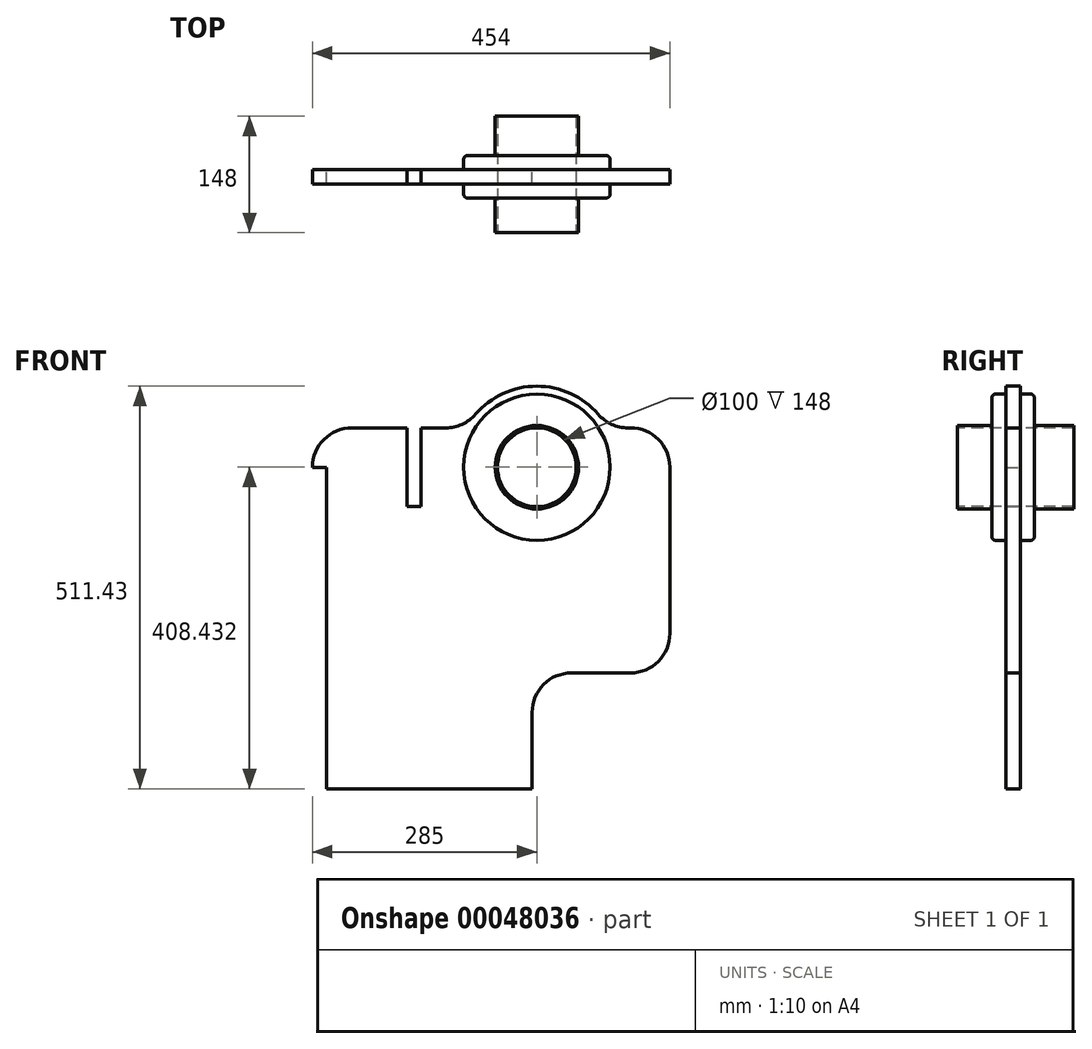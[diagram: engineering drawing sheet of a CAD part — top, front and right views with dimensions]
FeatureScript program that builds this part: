
annotation { "Feature Type Name" : "Feature", "Feature Type Description" : "" }
export const myFeature = defineFeature(function(context is Context, id is Id, definition is map)
    precondition{}
    {
        {
            var Q0;
            Q0=qCreatedBy(makeId("Front.planeOp"),FACE);
            var sketch = newSketch(context, id + "F0", { "sketchPlane" : qUnion([Q0])});
            skLineSegment(sketch, "E0", {"start": v(261, 333.88) * mm, "end": v(261, 431) * mm});
            skLineSegment(sketch, "E1", {"start": v(311, 481) * mm, "end": v(386, 481) * mm});
            skLineSegment(sketch, "E2.trimOffspring", {"start": v(436, 531) * mm, "end": v(436, 742.31) * mm});
            skLineSegment(sketch, "E3.0", {"start": v(32, 792.31) * mm, "end": v(102, 792.31) * mm});
            skCircle(sketch, "E4", {"center": v(267, 742.31) * mm, "radius": 53 * mm});
            skArc(sketch, "E5.0", {"start": v(344.96, 809.63) * mm, "mid": v(267, 845.31) * mm, "end": v(189.04, 809.63) * mm});
            skLineSegment(sketch, "E6.trimOffspring", {"start": v(382.8, 792.31) * mm, "end": v(386, 792.31) * mm});
            skPoint(sketch, "E7.visualSharp", {"position": v(357.05, 792.31) * mm});
            skArc(sketch, "E7.filletArc", {"start": v(344.96, 809.63) * mm, "mid": v(361.99, 796.85) * mm, "end": v(382.8, 792.31) * mm});
            skPoint(sketch, "E8.visualSharp", {"position": v(176.95, 792.31) * mm});
            skArc(sketch, "E8.filletArc", {"start": v(151.2, 792.31) * mm, "mid": v(172.01, 796.85) * mm, "end": v(189.04, 809.63) * mm});
            skPoint(sketch, "E9.visualSharp", {"position": v(436, 792.31) * mm});
            skArc(sketch, "E9.filletArc", {"start": v(436, 742.31) * mm, "mid": v(421.36, 777.67) * mm, "end": v(386, 792.31) * mm});
            skPoint(sketch, "E10.visualSharp", {"position": v(436, 481) * mm});
            skArc(sketch, "E10.filletArc", {"start": v(386, 481) * mm, "mid": v(421.36, 495.64) * mm, "end": v(436, 531) * mm});
            skPoint(sketch, "E11.visualSharp", {"position": v(261, 481) * mm});
            skArc(sketch, "E11.filletArc", {"start": v(311, 481) * mm, "mid": v(275.64, 466.36) * mm, "end": v(261, 431) * mm});
            skPoint(sketch, "E12.visualSharp", {"position": v(261, 446.37) * mm});
            skLineSegment(sketch, "E13", {"start": v(102, 792.31) * mm, "end": v(102, 692.31) * mm});
            skLineSegment(sketch, "E14", {"start": v(120, 792.31) * mm, "end": v(120, 692.31) * mm});
            skLineSegment(sketch, "E15", {"start": v(120, 692.31) * mm, "end": v(102, 692.31) * mm});
            skLineSegment(sketch, "E16.trimOffspring", {"start": v(120, 792.31) * mm, "end": v(151.2, 792.31) * mm});
            skLineSegment(sketch, "E17", {"start": v(0, 333.88) * mm, "end": v(0, 741.88) * mm});
            skLineSegment(sketch, "E18.0", {"start": v(0, 333.88) * mm, "end": v(261, 333.88) * mm});
            skLineSegment(sketch, "E19", {"start": v(0, 741.88) * mm, "end": v(-18, 741.88) * mm});
            skLineSegment(sketch, "E20", {"start": v(-18, 742.31) * mm, "end": v(-18, 741.88) * mm});
            skPoint(sketch, "E21.visualSharp", {"position": v(-18, 792.31) * mm});
            skArc(sketch, "E21.filletArc", {"start": v(32, 792.31) * mm, "mid": v(-3.36, 777.67) * mm, "end": v(-18, 742.31) * mm});
            skPoint(sketch, "E22.right.end.orphan", {"position": v(436, 446.37) * mm});
            skSolve(sketch);
        }
        {
            var Q0;
            Q0 = qSketchRegion(id + "F0", true);
            extrude(context, id + "F1", {"entities" : qUnion([Q0]), "depth" : 18 * mm});
        }
        {
            var Q0;
            Q0=makeQuery(id+"F1.opExtrude","CAP_FACE",FACE,{"disambiguationData":[OSD([sQuery(id+"F0.wireOp",EDGE,"E22.bottom"),sQuery(id+"F0.wireOp",EDGE,"E22.left"),sQuery(id+"F0.wireOp",EDGE,"E22.right"),sQuery(id+"F0.wireOp",EDGE,"9340d6fc-de35-4576-8b29-9b64dd72a72c"),sQuery(id+"F0.wireOp",EDGE,"ba2b4bda-3cf2-4f29-995d-d867b2875ad6"),sQuery(id+"F0.wireOp",EDGE,"E0"),sQuery(id+"F0.wireOp",EDGE,"E1"),sQuery(id+"F0.wireOp",EDGE,"E2.trimOffspring"),sQuery(id+"F0.wireOp",EDGE,"1ba28aa8-3367-4210-a1af-1df5a81b962f.filletArc"),sQuery(id+"F0.wireOp",EDGE,"E3.0"),sQuery(id+"F0.wireOp",EDGE,"E4"),sQuery(id+"F0.wireOp",EDGE,"E5.0")])],"isStart":true});
            var sketch = newSketch(context, id + "F2", { "sketchPlane" : qUnion([Q0])});
            skCircle(sketch, "E23.0", {"center": v(-267, 742.31) * mm, "radius": 53 * mm});
            skCircle(sketch, "E24.0", {"center": v(-267, 742.31) * mm, "radius": 50 * mm});
            skSolve(sketch);
        }
        {
            var Q0;
            Q0 = qSketchRegion(id + "F2", true);
            extrude(context, id + "F3", {"entities" : qUnion([Q0]), "operationType" : NewBodyOperationType.ADD, "depth" : 68 * mm, "hasSecondDirection" : true, "secondDirectionOppositeDirection" : true, "secondDirectionDepth" : 80 * mm});
        }
        {
            var Q0;
            Q0=makeQuery(id+"F1.opExtrude","CAP_FACE",FACE,{"disambiguationData":[OSD([sQuery(id+"F0.wireOp",EDGE,"E22.bottom"),sQuery(id+"F0.wireOp",EDGE,"E22.left"),sQuery(id+"F0.wireOp",EDGE,"E22.right"),sQuery(id+"F0.wireOp",EDGE,"9340d6fc-de35-4576-8b29-9b64dd72a72c"),sQuery(id+"F0.wireOp",EDGE,"ba2b4bda-3cf2-4f29-995d-d867b2875ad6"),sQuery(id+"F0.wireOp",EDGE,"E0"),sQuery(id+"F0.wireOp",EDGE,"E1"),sQuery(id+"F0.wireOp",EDGE,"E2.trimOffspring"),sQuery(id+"F0.wireOp",EDGE,"1ba28aa8-3367-4210-a1af-1df5a81b962f.filletArc"),sQuery(id+"F0.wireOp",EDGE,"E3.0"),sQuery(id+"F0.wireOp",EDGE,"E4"),sQuery(id+"F0.wireOp",EDGE,"E5.0")])],"isStart":true});
            var sketch = newSketch(context, id + "F4", { "sketchPlane" : qUnion([Q0])});
            skCircle(sketch, "E25.0", {"center": v(-267, 742.31) * mm, "radius": 53 * mm});
            skCircle(sketch, "E26.0", {"center": v(-267, 742.31) * mm, "radius": 93 * mm});
            skSolve(sketch);
        }
        {
            var Q0;
            Q0 = qSketchRegion(id + "F4", true);
            extrude(context, id + "F5", {"entities" : qUnion([Q0]), "operationType" : NewBodyOperationType.ADD, "depth" : 18 * mm});
        }
        {
            var Q0;
            Q0=makeQuery(id+"F1.opExtrude","CAP_FACE",FACE,{"disambiguationData":[OSD([sQuery(id+"F0.wireOp",EDGE,"E22.bottom"),sQuery(id+"F0.wireOp",EDGE,"E22.left"),sQuery(id+"F0.wireOp",EDGE,"E22.right"),sQuery(id+"F0.wireOp",EDGE,"9340d6fc-de35-4576-8b29-9b64dd72a72c"),sQuery(id+"F0.wireOp",EDGE,"ba2b4bda-3cf2-4f29-995d-d867b2875ad6"),sQuery(id+"F0.wireOp",EDGE,"E0"),sQuery(id+"F0.wireOp",EDGE,"E1"),sQuery(id+"F0.wireOp",EDGE,"E2.trimOffspring"),sQuery(id+"F0.wireOp",EDGE,"1ba28aa8-3367-4210-a1af-1df5a81b962f.filletArc"),sQuery(id+"F0.wireOp",EDGE,"E3.0"),sQuery(id+"F0.wireOp",EDGE,"E4"),sQuery(id+"F0.wireOp",EDGE,"E5.0")])],"isStart":false});
            var sketch = newSketch(context, id + "F6", { "sketchPlane" : qUnion([Q0])});
            skCircle(sketch, "E27.0", {"center": v(267, 742.31) * mm, "radius": 53 * mm});
            skCircle(sketch, "E28.0", {"center": v(267, 742.31) * mm, "radius": 93 * mm});
            skSolve(sketch);
        }
        {
            var Q0;
            Q0 = qSketchRegion(id + "F6", true);
            extrude(context, id + "F7", {"entities" : qUnion([Q0]), "operationType" : NewBodyOperationType.ADD, "depth" : 18 * mm});
        }
        {
            var Q0;
            Q0=makeQuery(id+"F5.opExtrude","CAP_EDGE",EDGE,{"disambiguationData":[OSD([sQuery(id+"F4.wireOp",EDGE,"E26.0")])],"isStart":false});
            var Q1;
            Q1=makeQuery(id+"F7.opExtrude","CAP_EDGE",EDGE,{"disambiguationData":[OSD([sQuery(id+"F6.wireOp",EDGE,"E28.0")])],"isStart":false});
            fillet(context, id + "F8", {"entities" : qUnion([Q0, Q1]), "radius" : 5 * mm, "tangentPropagation" : true, "allowEdgeOverflow" : false});
        }
    });
